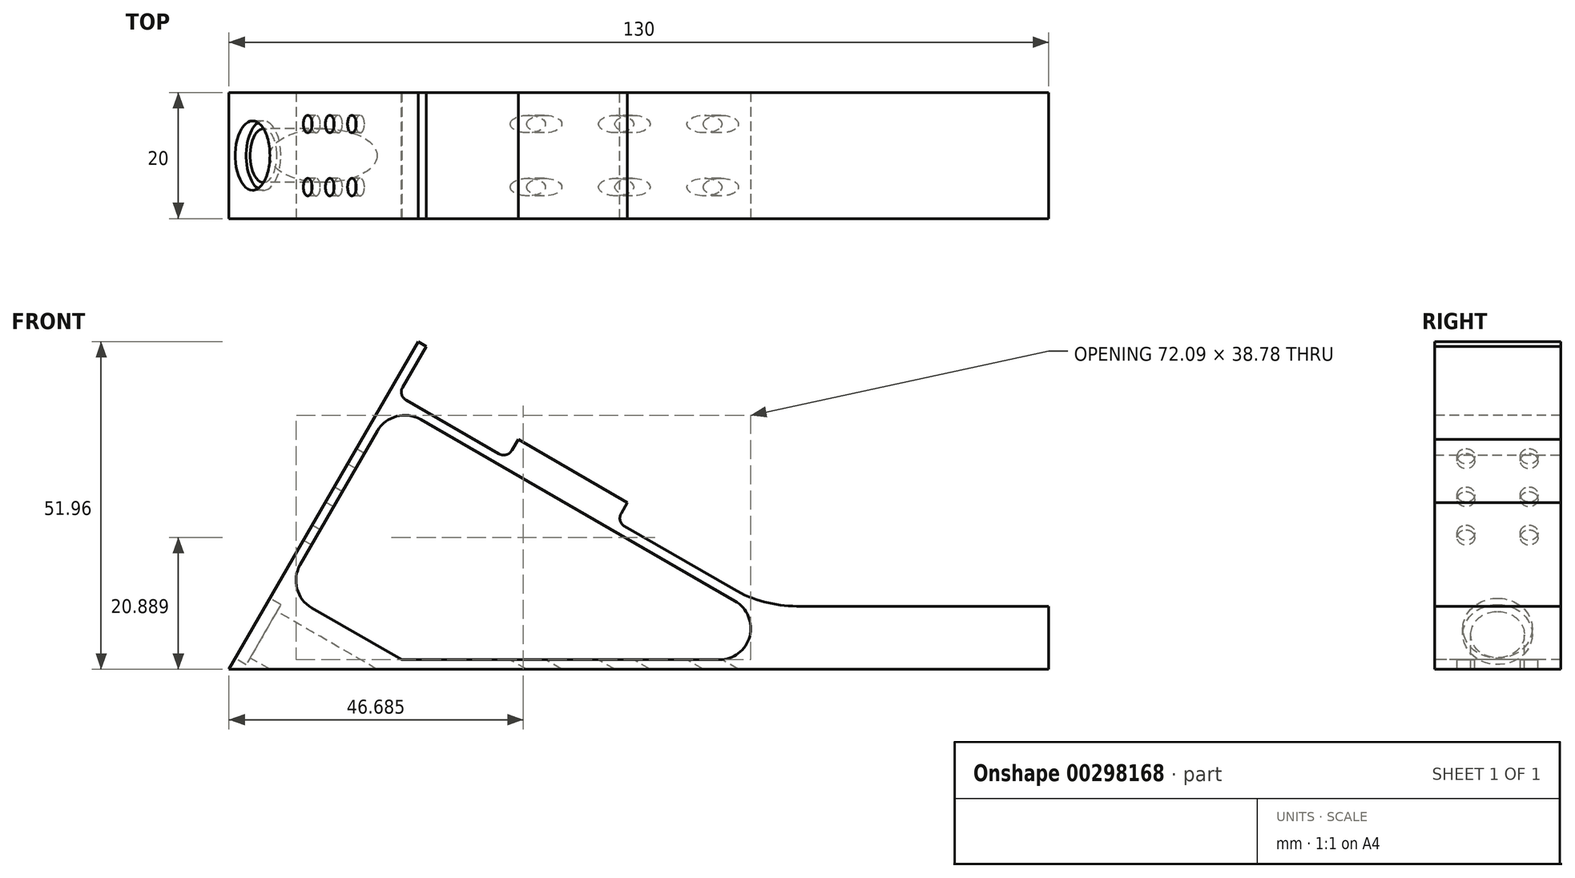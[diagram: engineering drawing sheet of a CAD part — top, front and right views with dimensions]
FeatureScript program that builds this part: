
annotation { "Feature Type Name" : "Feature", "Feature Type Description" : "" }
export const myFeature = defineFeature(function(context is Context, id is Id, definition is map)
    precondition{}
    {
        {
            var Q0;
            Q0=qCreatedBy(makeId("Front.planeOp"),FACE);
            var sketch = newSketch(context, id + "F0", { "sketchPlane" : qUnion([Q0])});
            skLineSegment(sketch, "E0", {"start": v(0, 0) * mm, "end": v(30, 51.96) * mm});
            skLineSegment(sketch, "E1", {"start": v(30, 51.96) * mm, "end": v(31.3, 51.21) * mm});
            skLineSegment(sketch, "E2", {"start": v(31.3, 51.21) * mm, "end": v(27.55, 44.72) * mm});
            skLineSegment(sketch, "E3", {"start": v(28.1, 42.67) * mm, "end": v(42.82, 34.17) * mm});
            skLineSegment(sketch, "E4", {"start": v(44.87, 34.72) * mm, "end": v(45.87, 36.45) * mm});
            skLineSegment(sketch, "E5", {"start": v(45.87, 36.45) * mm, "end": v(63.2, 26.45) * mm});
            skLineSegment(sketch, "E6", {"start": v(63.2, 26.45) * mm, "end": v(62.2, 24.72) * mm});
            skLineSegment(sketch, "E7", {"start": v(62.74, 22.67) * mm, "end": v(80.04, 12.68) * mm});
            skLineSegment(sketch, "E8", {"start": v(90.04, 10) * mm, "end": v(130, 10) * mm});
            skLineSegment(sketch, "E9", {"start": v(130, 10) * mm, "end": v(130, 0) * mm});
            skLineSegment(sketch, "E10", {"start": v(130, 0) * mm, "end": v(0, 0) * mm});
            skPoint(sketch, "E11.visualSharp", {"position": v(26.8, 43.42) * mm});
            skArc(sketch, "E11.filletArc", {"start": v(27.55, 44.72) * mm, "mid": v(27.4, 43.58) * mm, "end": v(28.1, 42.67) * mm});
            skPoint(sketch, "E12.visualSharp", {"position": v(44.12, 33.42) * mm});
            skArc(sketch, "E12.filletArc", {"start": v(42.82, 34.17) * mm, "mid": v(43.96, 34.02) * mm, "end": v(44.87, 34.72) * mm});
            skPoint(sketch, "E13.visualSharp", {"position": v(61.44, 23.42) * mm});
            skArc(sketch, "E13.filletArc", {"start": v(62.2, 24.72) * mm, "mid": v(62.04, 23.58) * mm, "end": v(62.74, 22.67) * mm});
            skPoint(sketch, "E14.visualSharp", {"position": v(84.68, 10) * mm});
            skArc(sketch, "E14.filletArc", {"start": v(80.04, 12.68) * mm, "mid": v(84.86, 10.68) * mm, "end": v(90.04, 10) * mm});
            skSolve(sketch);
        }
        {
            var Q0;
            Q0=makeQuery(id+"F0.imprint","IMPRINT",FACE,{"disambiguationData":[TD([[makeQuery(id+"F0.imprint","IMPRINT",EDGE,{"derivedFrom":sQuery(id+"F0.wireOp",EDGE,"E0")}),-1.0]])]});
            extrude(context, id + "F1", {"entities" : qUnion([Q0]), "endBound" : BoundingType.SYMMETRIC, "depth" : 20 * mm});
        }
        {
            var Q0;
            Q0=makeQuery(id+"F1.opExtrude","CAP_FACE",FACE,{"disambiguationData":[OSD([sQuery(id+"F0.wireOp",EDGE,"E0"),sQuery(id+"F0.wireOp",EDGE,"E1"),sQuery(id+"F0.wireOp",EDGE,"E2"),sQuery(id+"F0.wireOp",EDGE,"E3"),sQuery(id+"F0.wireOp",EDGE,"E4"),sQuery(id+"F0.wireOp",EDGE,"E5"),sQuery(id+"F0.wireOp",EDGE,"E6"),sQuery(id+"F0.wireOp",EDGE,"E7"),sQuery(id+"F0.wireOp",EDGE,"E8"),sQuery(id+"F0.wireOp",EDGE,"E9"),sQuery(id+"F0.wireOp",EDGE,"E10"),sQuery(id+"F0.wireOp",EDGE,"E11.filletArc"),sQuery(id+"F0.wireOp",EDGE,"E12.filletArc"),sQuery(id+"F0.wireOp",EDGE,"E13.filletArc"),sQuery(id+"F0.wireOp",EDGE,"E14.filletArc")])],"isStart":false});
            var sketch = newSketch(context, id + "F2", { "sketchPlane" : qUnion([Q0])});
            skLineSegment(sketch, "E15", {"start": v(23.55, 37.79) * mm, "end": v(11.3, 16.57) * mm});
            skLineSegment(sketch, "E16", {"start": v(13.13, 9.74) * mm, "end": v(27.4, 1.5) * mm});
            skLineSegment(sketch, "E17", {"start": v(27.4, 1.5) * mm, "end": v(77.74, 1.5) * mm});
            skLineSegment(sketch, "E18", {"start": v(80.24, 10.83) * mm, "end": v(30.38, 39.62) * mm});
            skPoint(sketch, "E19.visualSharp", {"position": v(26.05, 42.12) * mm});
            skArc(sketch, "E19.filletArc", {"start": v(30.38, 39.62) * mm, "mid": v(26.59, 40.12) * mm, "end": v(23.55, 37.79) * mm});
            skPoint(sketch, "E20.visualSharp", {"position": v(8.8, 12.24) * mm});
            skArc(sketch, "E20.filletArc", {"start": v(11.3, 16.57) * mm, "mid": v(10.8, 12.78) * mm, "end": v(13.13, 9.74) * mm});
            skPoint(sketch, "E21.visualSharp", {"position": v(96.4, 1.5) * mm});
            skArc(sketch, "E21.filletArc", {"start": v(77.74, 1.5) * mm, "mid": v(82.57, 5.2) * mm, "end": v(80.24, 10.83) * mm});
            skSolve(sketch);
        }
        {
            var Q0;
            Q0=makeQuery(id+"F2.imprint","IMPRINT",FACE,{"disambiguationData":[TD([[makeQuery(id+"F2.imprint","IMPRINT",EDGE,{"derivedFrom":sQuery(id+"F2.wireOp",EDGE,"E15")}),1.0]])]});
            extrude(context, id + "F3", {"entities" : qUnion([Q0]), "operationType" : NewBodyOperationType.REMOVE, "oppositeDirection" : true, "depth" : 20 * mm});
        }
        {
            var Q0;
            Q0=makeQuery(id+"F1.opExtrude","SWEPT_FACE",FACE,{"disambiguationData":[OSD([sQuery(id+"F0.wireOp",EDGE,"E0")])]});
            var sketch = newSketch(context, id + "F4", { "sketchPlane" : qUnion([Q0])});
            skCircle(sketch, "E22", {"center": v(0, 7.5) * mm, "radius": 4.25 * mm});
            skCircle(sketch, "E23", {"center": v(-5, 25) * mm, "radius": 1.4 * mm});
            skCircle(sketch, "E24", {"center": v(-5, 32) * mm, "radius": 1.4 * mm});
            skCircle(sketch, "E25", {"center": v(-5, 39) * mm, "radius": 1.4 * mm});
            skCircle(sketch, "E26", {"center": v(5, 39) * mm, "radius": 1.4 * mm});
            skCircle(sketch, "E27", {"center": v(5, 32) * mm, "radius": 1.4 * mm});
            skCircle(sketch, "E28", {"center": v(5, 25) * mm, "radius": 1.4 * mm});
            skCircle(sketch, "E29", {"center": v(0, 7.5) * mm, "radius": 5.5 * mm});
            skSolve(sketch);
        }
        {
            var Q0;
            Q0=makeQuery(id+"F4.imprint","IMPRINT",FACE,{"disambiguationData":[TD([[makeQuery(id+"F4.imprint","IMPRINT",EDGE,{"derivedFrom":sQuery(id+"F4.wireOp",EDGE,"E22")}),1.0]])]});
            extrude(context, id + "F5", {"entities" : qUnion([Q0]), "operationType" : NewBodyOperationType.REMOVE, "endBound" : BoundingType.THROUGH_ALL, "oppositeDirection" : true, "depth" : 25 * mm});
        }
        {
            var Q0;
            Q0=makeQuery(id+"F4.imprint","IMPRINT",FACE,{"disambiguationData":[TD([[makeQuery(id+"F4.imprint","IMPRINT",EDGE,{"derivedFrom":sQuery(id+"F4.wireOp",EDGE,"E22")}),-1.0]])]});
            extrude(context, id + "F6", {"entities" : qUnion([Q0]), "operationType" : NewBodyOperationType.REMOVE, "oppositeDirection" : true, "depth" : 2 * mm});
        }
        {
            var Q0;
            Q0=makeQuery(id+"F4.imprint","IMPRINT",FACE,{"disambiguationData":[TD([[makeQuery(id+"F4.imprint","IMPRINT",EDGE,{"derivedFrom":sQuery(id+"F4.wireOp",EDGE,"E23")}),1.0]])]});
            var Q1;
            Q1=makeQuery(id+"F4.imprint","IMPRINT",FACE,{"disambiguationData":[TD([[makeQuery(id+"F4.imprint","IMPRINT",EDGE,{"derivedFrom":sQuery(id+"F4.wireOp",EDGE,"E27")}),1.0]])]});
            var Q2;
            Q2=makeQuery(id+"F4.imprint","IMPRINT",FACE,{"disambiguationData":[TD([[makeQuery(id+"F4.imprint","IMPRINT",EDGE,{"derivedFrom":sQuery(id+"F4.wireOp",EDGE,"E24")}),1.0]])]});
            var Q3;
            Q3=makeQuery(id+"F4.imprint","IMPRINT",FACE,{"disambiguationData":[TD([[makeQuery(id+"F4.imprint","IMPRINT",EDGE,{"derivedFrom":sQuery(id+"F4.wireOp",EDGE,"E26")}),1.0]])]});
            var Q4;
            Q4=makeQuery(id+"F4.imprint","IMPRINT",FACE,{"disambiguationData":[TD([[makeQuery(id+"F4.imprint","IMPRINT",EDGE,{"derivedFrom":sQuery(id+"F4.wireOp",EDGE,"E25")}),1.0]])]});
            var Q5;
            Q5=makeQuery(id+"F4.imprint","IMPRINT",FACE,{"disambiguationData":[TD([[makeQuery(id+"F4.imprint","IMPRINT",EDGE,{"derivedFrom":sQuery(id+"F4.wireOp",EDGE,"E28")}),1.0]])]});
            extrude(context, id + "F7", {"entities" : qUnion([Q0, Q1, Q2, Q3, Q4, Q5]), "operationType" : NewBodyOperationType.REMOVE, "endBound" : BoundingType.THROUGH_ALL, "oppositeDirection" : true, "depth" : 25 * mm});
        }
    });
